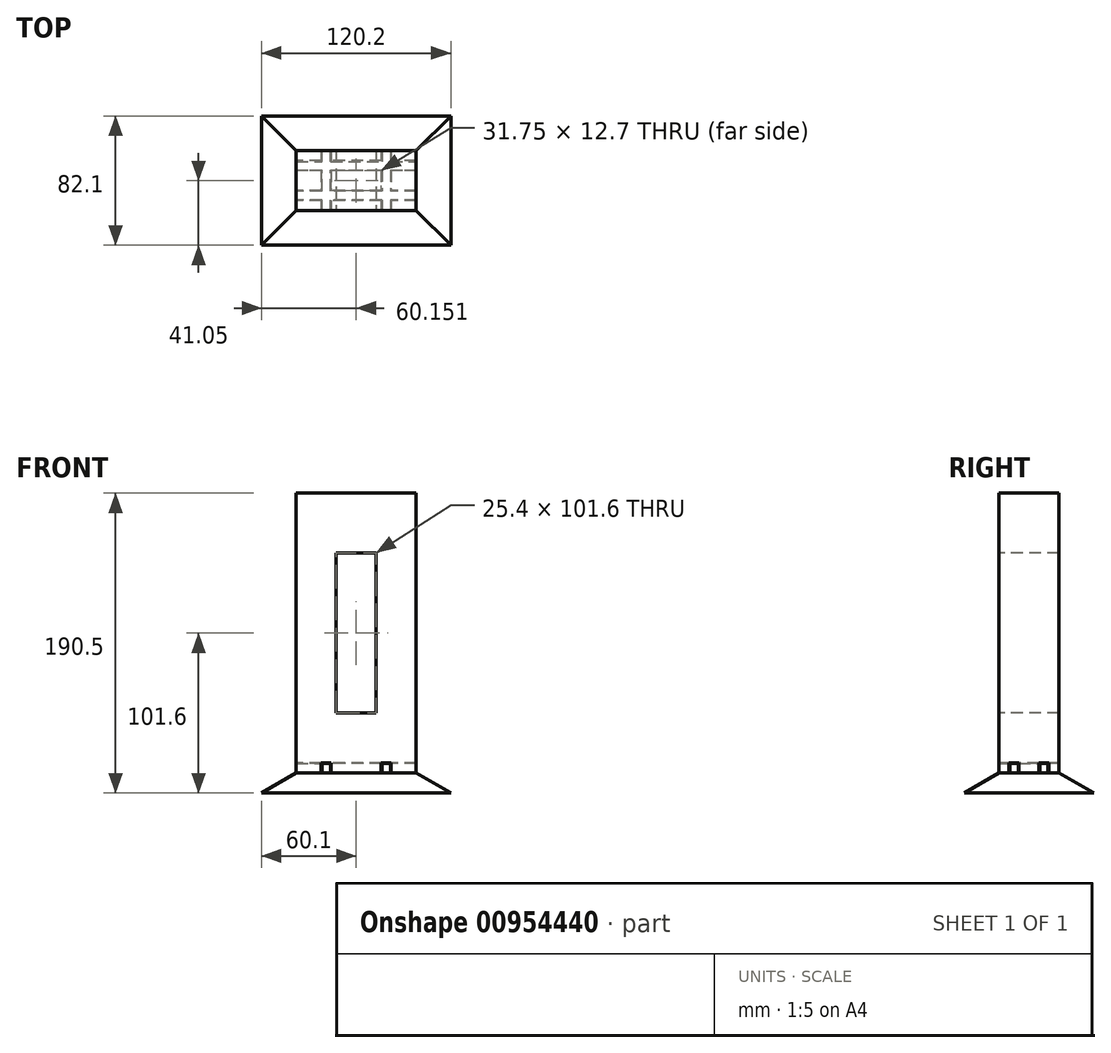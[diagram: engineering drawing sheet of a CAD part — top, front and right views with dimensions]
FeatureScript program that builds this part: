
annotation { "Feature Type Name" : "Feature", "Feature Type Description" : "" }
export const myFeature = defineFeature(function(context is Context, id is Id, definition is map)
    precondition{}
    {
        {
            var Q0;
            Q0=qCreatedBy(makeId("Front.planeOp"),FACE);
            var sketch = newSketch(context, id + "F0", { "sketchPlane" : qUnion([Q0])});
            skLineSegment(sketch, "E0.bottom", {"start": v(0, 0) * mm, "end": v(76.2, 0) * mm});
            skLineSegment(sketch, "E0.top", {"start": v(0, 177.8) * mm, "end": v(76.2, 177.8) * mm});
            skLineSegment(sketch, "E0.left", {"start": v(0, 0) * mm, "end": v(0, 177.8) * mm});
            skLineSegment(sketch, "E0.right", {"start": v(76.2, 0) * mm, "end": v(76.2, 177.8) * mm});
            skLineSegment(sketch, "E1.bottom", {"start": v(25.4, 139.7) * mm, "end": v(50.8, 139.7) * mm});
            skLineSegment(sketch, "E1.top", {"start": v(25.4, 38.1) * mm, "end": v(50.8, 38.1) * mm});
            skLineSegment(sketch, "E1.left", {"start": v(25.4, 139.7) * mm, "end": v(25.4, 38.1) * mm});
            skLineSegment(sketch, "E1.right", {"start": v(50.8, 139.7) * mm, "end": v(50.8, 38.1) * mm});
            skLineSegment(sketch, "E2.bottom", {"start": v(15.93, 0) * mm, "end": v(22.28, 0) * mm});
            skLineSegment(sketch, "E2.top", {"start": v(15.93, 6.35) * mm, "end": v(22.28, 6.35) * mm});
            skLineSegment(sketch, "E2.left", {"start": v(15.93, 0) * mm, "end": v(15.93, 6.35) * mm});
            skLineSegment(sketch, "E2.right", {"start": v(22.28, 0) * mm, "end": v(22.28, 6.35) * mm});
            skLineSegment(sketch, "E3.bottom", {"start": v(54.03, 0) * mm, "end": v(60.38, 0) * mm});
            skLineSegment(sketch, "E3.top", {"start": v(54.03, 6.35) * mm, "end": v(60.38, 6.35) * mm});
            skLineSegment(sketch, "E3.left", {"start": v(54.03, 0) * mm, "end": v(54.03, 6.35) * mm});
            skLineSegment(sketch, "E3.right", {"start": v(60.38, 0) * mm, "end": v(60.38, 6.35) * mm});
            skSolve(sketch);
        }
        {
            var Q0;
            Q0=makeQuery(id+"F0.imprint","IMPRINT",FACE,{"disambiguationData":[TD([[makeQuery(id+"F0.imprint","IMPRINT",EDGE,{"derivedFrom":sQuery(id+"F0.wireOp",EDGE,"E0.bottom")}),1.0]])]});
            extrude(context, id + "F1", {"entities" : qUnion([Q0]), "oppositeDirection" : true, "depth" : 38.1 * mm, "offsetDistance" : 25.4 * mm});
        }
        {
            var Q0;
            Q0=makeQuery(id+"F1.opExtrude","SWEPT_FACE",FACE,{"disambiguationData":[OSD([sQuery(id+"F0.wireOp",EDGE,"E0.left")])]});
            var sketch = newSketch(context, id + "F2", { "sketchPlane" : qUnion([Q0])});
            skLineSegment(sketch, "E4.bottom", {"start": v(-31.75, 0) * mm, "end": v(-25.4, 0) * mm});
            skLineSegment(sketch, "E4.top", {"start": v(-31.75, 6.35) * mm, "end": v(-25.4, 6.35) * mm});
            skLineSegment(sketch, "E4.left", {"start": v(-31.75, 0) * mm, "end": v(-31.75, 6.35) * mm});
            skLineSegment(sketch, "E4.right", {"start": v(-25.4, 0) * mm, "end": v(-25.4, 6.35) * mm});
            skLineSegment(sketch, "E5.bottom", {"start": v(-12.7, 0) * mm, "end": v(-6.35, 0) * mm});
            skLineSegment(sketch, "E5.top", {"start": v(-12.7, 6.35) * mm, "end": v(-6.35, 6.35) * mm});
            skLineSegment(sketch, "E5.left", {"start": v(-12.7, 0) * mm, "end": v(-12.7, 6.35) * mm});
            skLineSegment(sketch, "E5.right", {"start": v(-6.35, 0) * mm, "end": v(-6.35, 6.35) * mm});
            skSolve(sketch);
        }
        {
            var Q0;
            Q0=makeQuery(id+"F2.imprint","IMPRINT",FACE,{"disambiguationData":[TD([[makeQuery(id+"F2.imprint","IMPRINT",EDGE,{"derivedFrom":sQuery(id+"F2.wireOp",EDGE,"E4.bottom")}),1.0]])]});
            var Q1;
            Q1=makeQuery(id+"F2.imprint","IMPRINT",FACE,{"disambiguationData":[TD([[makeQuery(id+"F2.imprint","IMPRINT",EDGE,{"derivedFrom":sQuery(id+"F2.wireOp",EDGE,"E5.bottom")}),1.0]])]});
            extrude(context, id + "F3", {"entities" : qUnion([Q0, Q1]), "operationType" : NewBodyOperationType.REMOVE, "endBound" : BoundingType.THROUGH_ALL, "oppositeDirection" : true, "depth" : 25.4 * mm, "offsetDistance" : 25.4 * mm});
        }
        {
            var Q0;
            Q0=qCreatedBy(makeId("Top.planeOp"),FACE);
            var sketch = newSketch(context, id + "F4", { "sketchPlane" : qUnion([Q0])});
            skLineSegment(sketch, "E6.0.0", {"start": v(54.03, 0) * mm, "end": v(54.03, 6.35) * mm, "construction": true});
            skLineSegment(sketch, "E6.0.1", {"start": v(54.03, 6.35) * mm, "end": v(22.28, 6.35) * mm, "construction": true});
            skLineSegment(sketch, "E6.0.2", {"start": v(22.28, 6.35) * mm, "end": v(22.28, 0) * mm, "construction": true});
            skLineSegment(sketch, "E6.0.3", {"start": v(22.28, 0) * mm, "end": v(15.93, 0) * mm, "construction": true});
            skLineSegment(sketch, "E6.0.4", {"start": v(15.93, 0) * mm, "end": v(15.93, 6.35) * mm, "construction": true});
            skLineSegment(sketch, "E6.0.5", {"start": v(15.93, 6.35) * mm, "end": v(0, 6.35) * mm, "construction": true});
            skLineSegment(sketch, "E6.0.6", {"start": v(0, 6.35) * mm, "end": v(0, 12.7) * mm, "construction": true});
            skLineSegment(sketch, "E6.0.7", {"start": v(0, 12.7) * mm, "end": v(15.93, 12.7) * mm, "construction": true});
            skLineSegment(sketch, "E6.0.8", {"start": v(15.93, 12.7) * mm, "end": v(15.93, 25.4) * mm, "construction": true});
            skLineSegment(sketch, "E6.0.9", {"start": v(15.93, 25.4) * mm, "end": v(0, 25.4) * mm, "construction": true});
            skLineSegment(sketch, "E6.0.10", {"start": v(0, 25.4) * mm, "end": v(0, 31.75) * mm, "construction": true});
            skLineSegment(sketch, "E6.0.11", {"start": v(0, 31.75) * mm, "end": v(15.93, 31.75) * mm, "construction": true});
            skLineSegment(sketch, "E6.0.12", {"start": v(15.93, 31.75) * mm, "end": v(15.93, 38.1) * mm, "construction": true});
            skLineSegment(sketch, "E6.0.13", {"start": v(15.93, 38.1) * mm, "end": v(22.28, 38.1) * mm, "construction": true});
            skLineSegment(sketch, "E6.0.14", {"start": v(22.28, 38.1) * mm, "end": v(22.28, 31.75) * mm, "construction": true});
            skLineSegment(sketch, "E6.0.15", {"start": v(22.28, 31.75) * mm, "end": v(54.03, 31.75) * mm, "construction": true});
            skLineSegment(sketch, "E6.0.16", {"start": v(54.03, 31.75) * mm, "end": v(54.03, 38.1) * mm, "construction": true});
            skLineSegment(sketch, "E6.0.17", {"start": v(54.03, 38.1) * mm, "end": v(60.38, 38.1) * mm, "construction": true});
            skLineSegment(sketch, "E6.0.18", {"start": v(60.38, 38.1) * mm, "end": v(60.38, 31.75) * mm, "construction": true});
            skLineSegment(sketch, "E6.0.19", {"start": v(60.38, 31.75) * mm, "end": v(76.2, 31.75) * mm, "construction": true});
            skLineSegment(sketch, "E6.0.20", {"start": v(76.2, 31.75) * mm, "end": v(76.2, 25.4) * mm, "construction": true});
            skLineSegment(sketch, "E6.0.21", {"start": v(76.2, 25.4) * mm, "end": v(60.38, 25.4) * mm, "construction": true});
            skLineSegment(sketch, "E6.0.22", {"start": v(60.38, 25.4) * mm, "end": v(60.38, 12.7) * mm, "construction": true});
            skLineSegment(sketch, "E6.0.23", {"start": v(60.38, 12.7) * mm, "end": v(76.2, 12.7) * mm, "construction": true});
            skLineSegment(sketch, "E6.0.24", {"start": v(76.2, 12.7) * mm, "end": v(76.2, 6.35) * mm, "construction": true});
            skLineSegment(sketch, "E6.0.25", {"start": v(76.2, 6.35) * mm, "end": v(60.38, 6.35) * mm, "construction": true});
            skLineSegment(sketch, "E6.0.26", {"start": v(60.38, 6.35) * mm, "end": v(60.38, 0) * mm, "construction": true});
            skLineSegment(sketch, "E6.0.27", {"start": v(60.38, 0) * mm, "end": v(54.03, 0) * mm, "construction": true});
            skLineSegment(sketch, "E7.0.0", {"start": v(54.03, 25.4) * mm, "end": v(54.03, 12.7) * mm, "construction": true});
            skLineSegment(sketch, "E7.0.1", {"start": v(54.03, 12.7) * mm, "end": v(22.28, 12.7) * mm, "construction": true});
            skLineSegment(sketch, "E7.0.2", {"start": v(22.28, 12.7) * mm, "end": v(22.28, 25.4) * mm, "construction": true});
            skLineSegment(sketch, "E7.0.3", {"start": v(22.28, 25.4) * mm, "end": v(54.03, 25.4) * mm, "construction": true});
            skLineSegment(sketch, "E8", {"start": v(19.1, 0) * mm, "end": v(19.1, 38.1) * mm, "construction": true});
            skLineSegment(sketch, "E9", {"start": v(57.2, 0) * mm, "end": v(57.2, 38.1) * mm, "construction": true});
            skLineSegment(sketch, "E10", {"start": v(0, 9.53) * mm, "end": v(76.2, 9.53) * mm, "construction": true});
            skLineSegment(sketch, "E11", {"start": v(0, 28.57) * mm, "end": v(76.2, 28.57) * mm, "construction": true});
            skLineSegment(sketch, "E12.bottom", {"start": v(16.3, 0) * mm, "end": v(21.9, 0) * mm});
            skLineSegment(sketch, "E12.top", {"start": v(16.3, 38.1) * mm, "end": v(21.9, 38.1) * mm});
            skLineSegment(sketch, "E12.left", {"start": v(16.3, 0) * mm, "end": v(16.3, 38.1) * mm});
            skLineSegment(sketch, "E12.right", {"start": v(21.9, 0) * mm, "end": v(21.9, 38.1) * mm});
            skLineSegment(sketch, "E13.bottom", {"start": v(54.4, 38.1) * mm, "end": v(60, 38.1) * mm});
            skLineSegment(sketch, "E13.top", {"start": v(54.4, 0) * mm, "end": v(60, 0) * mm});
            skLineSegment(sketch, "E13.left", {"start": v(54.4, 38.1) * mm, "end": v(54.4, 0) * mm});
            skLineSegment(sketch, "E13.right", {"start": v(60, 38.1) * mm, "end": v(60, 0) * mm});
            skLineSegment(sketch, "E14.bottom", {"start": v(76.2, 6.73) * mm, "end": v(0, 6.73) * mm});
            skLineSegment(sketch, "E14.top", {"start": v(76.2, 12.32) * mm, "end": v(0, 12.32) * mm});
            skLineSegment(sketch, "E14.left", {"start": v(76.2, 6.73) * mm, "end": v(76.2, 12.32) * mm});
            skLineSegment(sketch, "E14.right", {"start": v(0, 6.73) * mm, "end": v(0, 12.32) * mm});
            skLineSegment(sketch, "E15.bottom", {"start": v(0, 25.78) * mm, "end": v(76.2, 25.78) * mm});
            skLineSegment(sketch, "E15.top", {"start": v(0, 31.12) * mm, "end": v(76.2, 31.12) * mm});
            skLineSegment(sketch, "E15.left", {"start": v(0, 25.78) * mm, "end": v(0, 31.12) * mm});
            skLineSegment(sketch, "E15.right", {"start": v(76.2, 25.78) * mm, "end": v(76.2, 31.12) * mm});
            skSolve(sketch);
        }
        {
            var Q0;
            {var subQ0=sQuery(id+"F4.wireOp",EDGE,"E12.bottom");Q0=makeQuery(id+"F4.imprint","IMPRINT",FACE,{"disambiguationData":[TD([[makeQuery(id+"F4.imprint","IMPRINT",EDGE,{"derivedFrom":subQ0}),1.0]])]});}
            var Q1;
            {var subQ0=sQuery(id+"F4.wireOp",EDGE,"E14.bottom");var subQ1=sQuery(id+"F4.wireOp",EDGE,"E12.left");var subQ2=makeQuery(id+"F4.imprint","INTERSECT",VERTEX,{"derivedFrom":[subQ1,subQ0]});Q1=makeQuery(id+"F4.imprint","IMPRINT",FACE,{"disambiguationData":[TD([[makeQuery(id+"F4.imprint","IMPRINT",EDGE,{"disambiguationData":[TD([[subQ2,-1.0]])],"derivedFrom":subQ1}),-1.0]])]});}
            var Q2;
            {var subQ5=sQuery(id+"F4.wireOp",EDGE,"E14.right");Q2=makeQuery(id+"F4.imprint","IMPRINT",FACE,{"disambiguationData":[TD([[makeQuery(id+"F4.imprint","IMPRINT",EDGE,{"derivedFrom":subQ5}),-1.0]])]});}
            var Q3;
            {var subQ0=sQuery(id+"F4.wireOp",EDGE,"E14.top");var subQ1=sQuery(id+"F4.wireOp",EDGE,"E12.left");var subQ2=makeQuery(id+"F4.imprint","INTERSECT",VERTEX,{"derivedFrom":[subQ1,subQ0]});Q3=makeQuery(id+"F4.imprint","IMPRINT",FACE,{"disambiguationData":[TD([[makeQuery(id+"F4.imprint","IMPRINT",EDGE,{"disambiguationData":[TD([[subQ2,-1.0]])],"derivedFrom":subQ1}),-1.0]])]});}
            var Q4;
            {var subQ0=sQuery(id+"F4.wireOp",EDGE,"E14.bottom");var subQ1=sQuery(id+"F4.wireOp",EDGE,"E12.right");var subQ2=makeQuery(id+"F4.imprint","INTERSECT",VERTEX,{"derivedFrom":[subQ1,subQ0]});Q4=makeQuery(id+"F4.imprint","IMPRINT",FACE,{"disambiguationData":[TD([[makeQuery(id+"F4.imprint","IMPRINT",EDGE,{"disambiguationData":[TD([[subQ2,-1.0]])],"derivedFrom":subQ1}),-1.0]])]});}
            var Q5;
            {var subQ0=sQuery(id+"F4.wireOp",EDGE,"E14.bottom");var subQ1=sQuery(id+"F4.wireOp",EDGE,"E13.left");var subQ2=makeQuery(id+"F4.imprint","INTERSECT",VERTEX,{"derivedFrom":[subQ1,subQ0]});Q5=makeQuery(id+"F4.imprint","IMPRINT",FACE,{"disambiguationData":[TD([[makeQuery(id+"F4.imprint","IMPRINT",EDGE,{"disambiguationData":[TD([[subQ2,1.0]])],"derivedFrom":subQ1}),1.0]])]});}
            var Q6;
            {var subQ0=sQuery(id+"F4.wireOp",EDGE,"E13.top");Q6=makeQuery(id+"F4.imprint","IMPRINT",FACE,{"disambiguationData":[TD([[makeQuery(id+"F4.imprint","IMPRINT",EDGE,{"derivedFrom":subQ0}),1.0]])]});}
            var Q7;
            {var subQ5=sQuery(id+"F4.wireOp",EDGE,"E14.left");Q7=makeQuery(id+"F4.imprint","IMPRINT",FACE,{"disambiguationData":[TD([[makeQuery(id+"F4.imprint","IMPRINT",EDGE,{"derivedFrom":subQ5}),1.0]])]});}
            var Q8;
            {var subQ0=sQuery(id+"F4.wireOp",EDGE,"E15.bottom");var subQ1=sQuery(id+"F4.wireOp",EDGE,"E13.left");var subQ2=makeQuery(id+"F4.imprint","INTERSECT",VERTEX,{"derivedFrom":[subQ1,subQ0]});Q8=makeQuery(id+"F4.imprint","IMPRINT",FACE,{"disambiguationData":[TD([[makeQuery(id+"F4.imprint","IMPRINT",EDGE,{"disambiguationData":[TD([[subQ2,-1.0]])],"derivedFrom":subQ1}),1.0]])]});}
            var Q9;
            {var subQ0=sQuery(id+"F4.wireOp",EDGE,"E15.top");var subQ1=sQuery(id+"F4.wireOp",EDGE,"E13.left");var subQ2=makeQuery(id+"F4.imprint","INTERSECT",VERTEX,{"derivedFrom":[subQ1,subQ0]});Q9=makeQuery(id+"F4.imprint","IMPRINT",FACE,{"disambiguationData":[TD([[makeQuery(id+"F4.imprint","IMPRINT",EDGE,{"disambiguationData":[TD([[subQ2,-1.0]])],"derivedFrom":subQ1}),1.0]])]});}
            var Q10;
            {var subQ5=sQuery(id+"F4.wireOp",EDGE,"E15.right");Q10=makeQuery(id+"F4.imprint","IMPRINT",FACE,{"disambiguationData":[TD([[makeQuery(id+"F4.imprint","IMPRINT",EDGE,{"derivedFrom":subQ5}),1.0]])]});}
            var Q11;
            {var subQ0=sQuery(id+"F4.wireOp",EDGE,"E13.bottom");Q11=makeQuery(id+"F4.imprint","IMPRINT",FACE,{"disambiguationData":[TD([[makeQuery(id+"F4.imprint","IMPRINT",EDGE,{"derivedFrom":subQ0}),-1.0]])]});}
            var Q12;
            {var subQ0=sQuery(id+"F4.wireOp",EDGE,"E15.top");var subQ1=sQuery(id+"F4.wireOp",EDGE,"E12.right");var subQ2=makeQuery(id+"F4.imprint","INTERSECT",VERTEX,{"derivedFrom":[subQ1,subQ0]});Q12=makeQuery(id+"F4.imprint","IMPRINT",FACE,{"disambiguationData":[TD([[makeQuery(id+"F4.imprint","IMPRINT",EDGE,{"disambiguationData":[TD([[subQ2,1.0]])],"derivedFrom":subQ1}),-1.0]])]});}
            var Q13;
            {var subQ0=sQuery(id+"F4.wireOp",EDGE,"E15.bottom");var subQ1=sQuery(id+"F4.wireOp",EDGE,"E12.left");var subQ2=makeQuery(id+"F4.imprint","INTERSECT",VERTEX,{"derivedFrom":[subQ1,subQ0]});Q13=makeQuery(id+"F4.imprint","IMPRINT",FACE,{"disambiguationData":[TD([[makeQuery(id+"F4.imprint","IMPRINT",EDGE,{"disambiguationData":[TD([[subQ2,-1.0]])],"derivedFrom":subQ1}),-1.0]])]});}
            var Q14;
            {var subQ0=sQuery(id+"F4.wireOp",EDGE,"E12.top");Q14=makeQuery(id+"F4.imprint","IMPRINT",FACE,{"disambiguationData":[TD([[makeQuery(id+"F4.imprint","IMPRINT",EDGE,{"derivedFrom":subQ0}),-1.0]])]});}
            var Q15;
            {var subQ5=sQuery(id+"F4.wireOp",EDGE,"E15.left");Q15=makeQuery(id+"F4.imprint","IMPRINT",FACE,{"disambiguationData":[TD([[makeQuery(id+"F4.imprint","IMPRINT",EDGE,{"derivedFrom":subQ5}),-1.0]])]});}
            extrude(context, id + "F5", {"entities" : qUnion([Q0, Q1, Q2, Q3, Q4, Q5, Q6, Q7, Q8, Q9, Q10, Q11, Q12, Q13, Q14, Q15]), "depth" : 6.1 * mm, "offsetDistance" : 25.4 * mm});
        }
        {
            var Q0;
            Q0=makeQuery(id+"F5.opExtrude","CAP_FACE",FACE,{"disambiguationData":[OSD([sQuery(id+"F4.wireOp",EDGE,"E12.bottom"),sQuery(id+"F4.wireOp",EDGE,"E12.top"),sQuery(id+"F4.wireOp",EDGE,"E12.left"),sQuery(id+"F4.wireOp",EDGE,"E12.right"),sQuery(id+"F4.wireOp",EDGE,"E13.bottom"),sQuery(id+"F4.wireOp",EDGE,"E13.top"),sQuery(id+"F4.wireOp",EDGE,"E13.left"),sQuery(id+"F4.wireOp",EDGE,"E13.right"),sQuery(id+"F4.wireOp",EDGE,"E14.bottom"),sQuery(id+"F4.wireOp",EDGE,"E14.top"),sQuery(id+"F4.wireOp",EDGE,"E14.left"),sQuery(id+"F4.wireOp",EDGE,"E14.right"),sQuery(id+"F4.wireOp",EDGE,"E15.bottom"),sQuery(id+"F4.wireOp",EDGE,"E15.top"),sQuery(id+"F4.wireOp",EDGE,"E15.left"),sQuery(id+"F4.wireOp",EDGE,"E15.right")])],"isStart":true});
            var sketch = newSketch(context, id + "F6", { "sketchPlane" : qUnion([Q0])});
            skPoint(sketch, "E16.oppositeSnap0", {"position": v(76.2, -28.45) * mm});
            skLineSegment(sketch, "E16.bottom", {"start": v(0, 0) * mm, "end": v(76.2, 0) * mm});
            skLineSegment(sketch, "E16.top", {"start": v(0, -38.1) * mm, "end": v(76.2, -38.1) * mm});
            skLineSegment(sketch, "E16.left", {"start": v(0, 0) * mm, "end": v(0, -38.1) * mm});
            skLineSegment(sketch, "E16.right", {"start": v(76.2, 0) * mm, "end": v(76.2, -38.1) * mm});
            skSolve(sketch);
        }
        {
            var Q0;
            Q0=qSketchRegion(id+"F6",true);
            extrude(context, id + "F7", {"entities" : qUnion([Q0]), "operationType" : NewBodyOperationType.ADD, "depth" : 12.7 * mm, "offsetDistance" : 25.4 * mm, "hasDraft" : true, "draftAngle" : 60 * degree});
        }
    });
